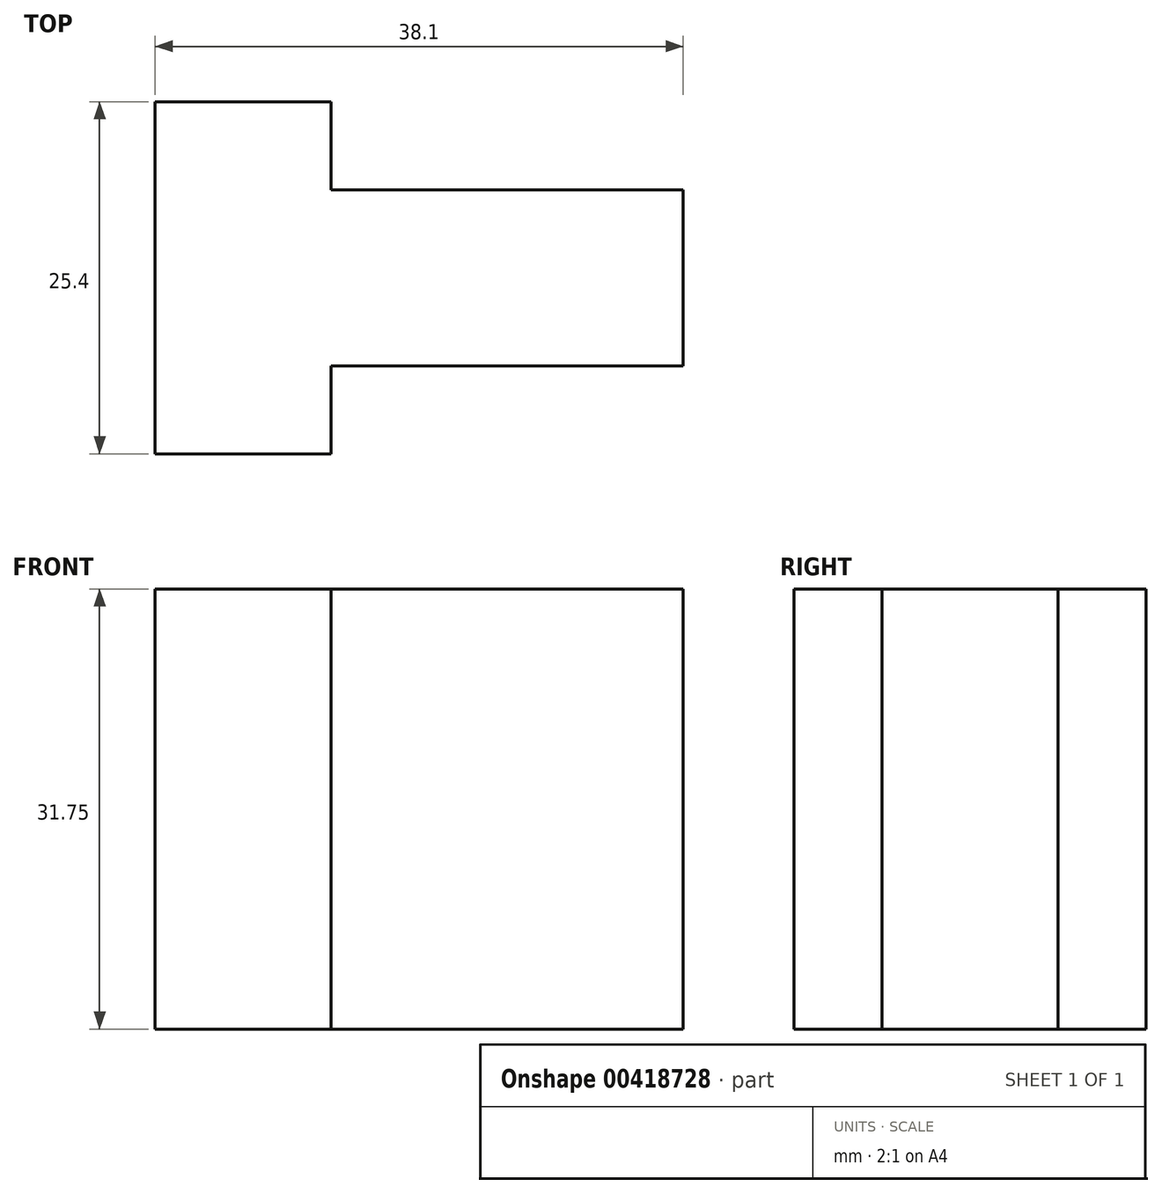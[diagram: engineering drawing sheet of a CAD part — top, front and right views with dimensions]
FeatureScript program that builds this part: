
annotation { "Feature Type Name" : "Feature", "Feature Type Description" : "" }
export const myFeature = defineFeature(function(context is Context, id is Id, definition is map)
    precondition{}
    {
        {
            var Q0;
            Q0=qCreatedBy(makeId("Top.planeOp"),FACE);
            var sketch = newSketch(context, id + "F0", { "sketchPlane" : qUnion([Q0])});
            skLineSegment(sketch, "E0", {"start": v(0, 0) * mm, "end": v(0, 25.4) * mm});
            skLineSegment(sketch, "E1", {"start": v(0, 25.4) * mm, "end": v(12.7, 25.4) * mm});
            skLineSegment(sketch, "E2", {"start": v(0, 0) * mm, "end": v(12.7, 0) * mm});
            skLineSegment(sketch, "E3", {"start": v(12.7, 25.4) * mm, "end": v(12.7, 19.05) * mm});
            skLineSegment(sketch, "E4", {"start": v(12.7, 0) * mm, "end": v(12.7, 6.35) * mm});
            skLineSegment(sketch, "E5", {"start": v(12.7, 6.35) * mm, "end": v(38.1, 6.35) * mm});
            skLineSegment(sketch, "E6", {"start": v(12.7, 19.05) * mm, "end": v(38.1, 19.05) * mm});
            skLineSegment(sketch, "E7", {"start": v(38.1, 19.05) * mm, "end": v(38.1, 6.35) * mm});
            skSolve(sketch);
        }
        {
            var Q0;
            Q0=makeQuery(id+"F0.imprint","IMPRINT",FACE,{"disambiguationData":[TD([[makeQuery(id+"F0.imprint","IMPRINT",EDGE,{"derivedFrom":sQuery(id+"F0.wireOp",EDGE,"E0")}),-1.0]])]});
            extrude(context, id + "F1", {"entities" : qUnion([Q0]), "depth" : 31.75 * mm});
        }
    });
